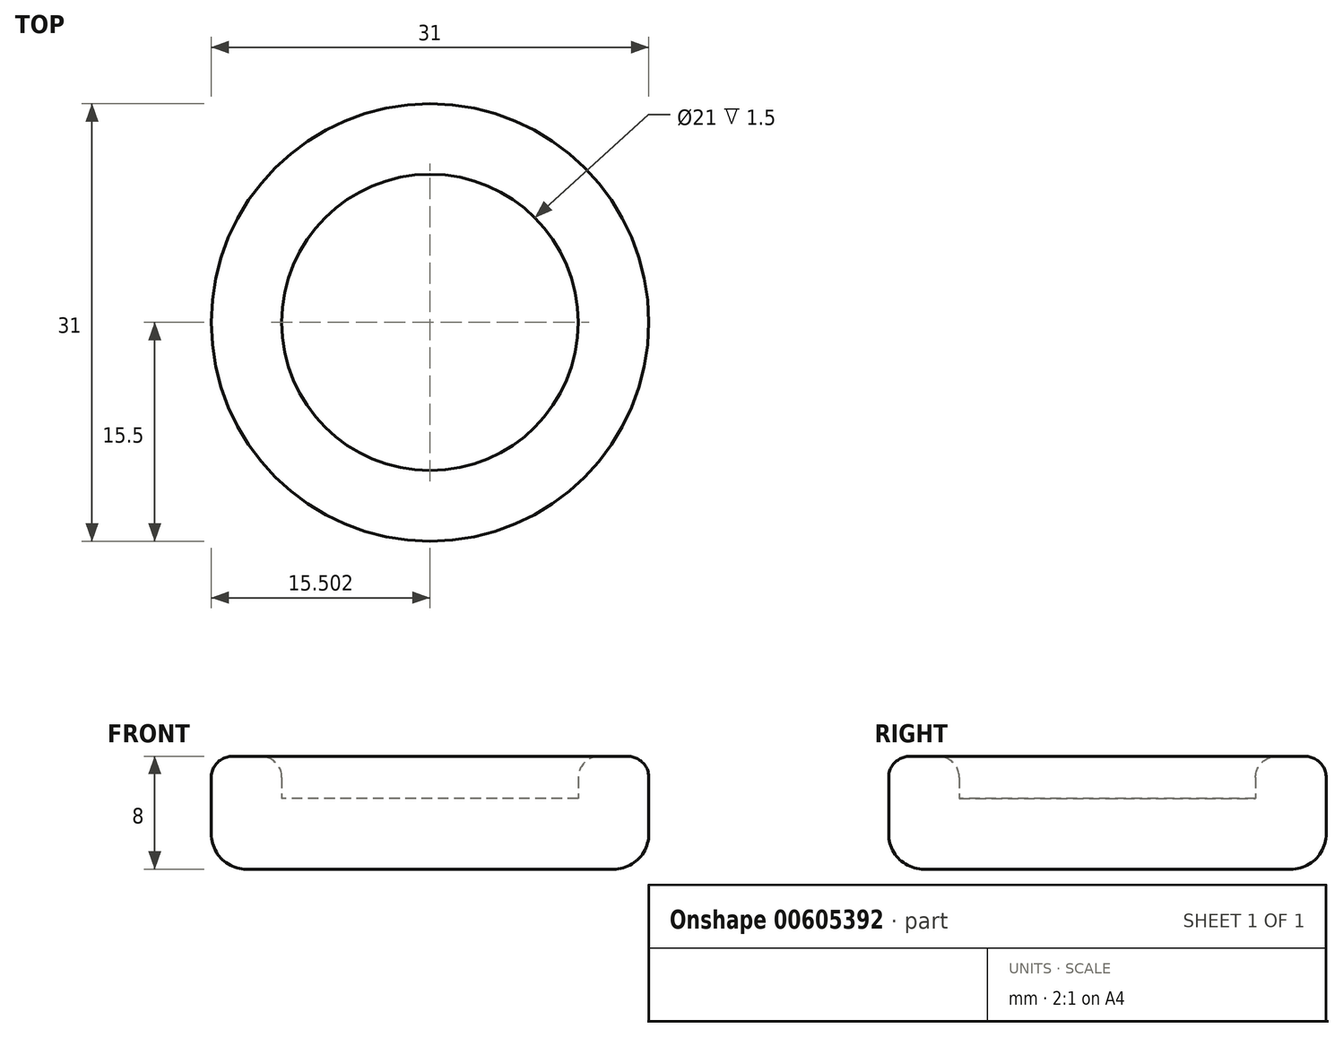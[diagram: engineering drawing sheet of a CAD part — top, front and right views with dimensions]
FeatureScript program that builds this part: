
annotation { "Feature Type Name" : "Feature", "Feature Type Description" : "" }
export const myFeature = defineFeature(function(context is Context, id is Id, definition is map)
    precondition{}
    {
        {
            var Q0;
            Q0=qCreatedBy(makeId("Top.planeOp"),FACE);
            var sketch = newSketch(context, id + "F0", { "sketchPlane" : qUnion([Q0])});
            skCircle(sketch, "E0", {"center": v(-13.35, 0) * mm, "radius": 15.5 * mm});
            skSolve(sketch);
        }
        {
            var Q0;
            Q0=makeQuery(id+"F0.imprint","IMPRINT",FACE,{"disambiguationData":[TD([[makeQuery(id+"F0.imprint","IMPRINT",EDGE,{"derivedFrom":sQuery(id+"F0.wireOp",EDGE,"E0")}),1.0]])]});
            extrude(context, id + "F1", {"entities" : qUnion([Q0]), "depth" : 8 * mm, "offsetDistance" : 25 * mm});
        }
        {
            var Q0;
            Q0=makeQuery(id+"F1.opExtrude","CAP_FACE",FACE,{"disambiguationData":[OSD([sQuery(id+"F0.wireOp",EDGE,"E0")])],"isStart":false});
            shell(context, id + "F2", {"entities" : qUnion([Q0]), "thickness" : 5 * mm});
        }
        {
            var Q0;
            Q0=makeQuery(id+"F1.opExtrude","CAP_EDGE",EDGE,{"disambiguationData":[OSD([sQuery(id+"F0.wireOp",EDGE,"E0")])],"isStart":false});
            var Q1;
            {var subQ0=sQuery(id+"F0.wireOp",EDGE,"E0");Q1=makeQuery(id+"F2.opShell","OFFSET_EDGE",EDGE,{"disambiguationData":[OSD([subQ0]),TDD([makeQuery(id+"F1.opExtrude","CAP_EDGE",EDGE,{"disambiguationData":[OSD([subQ0])],"isStart":false})])]});}
            fillet(context, id + "F3", {"entities" : qUnion([Q0, Q1]), "radius" : 1.5 * mm, "tangentPropagation" : true, "allowEdgeOverflow" : false});
        }
        {
            var Q0;
            Q0=makeQuery(id+"F1.opExtrude","CAP_FACE",FACE,{"disambiguationData":[OSD([sQuery(id+"F0.wireOp",EDGE,"E0")])],"isStart":true});
            fillet(context, id + "F4", {"entities" : qUnion([Q0]), "radius" : 2.5 * mm, "tangentPropagation" : true, "allowEdgeOverflow" : false});
        }
    });
